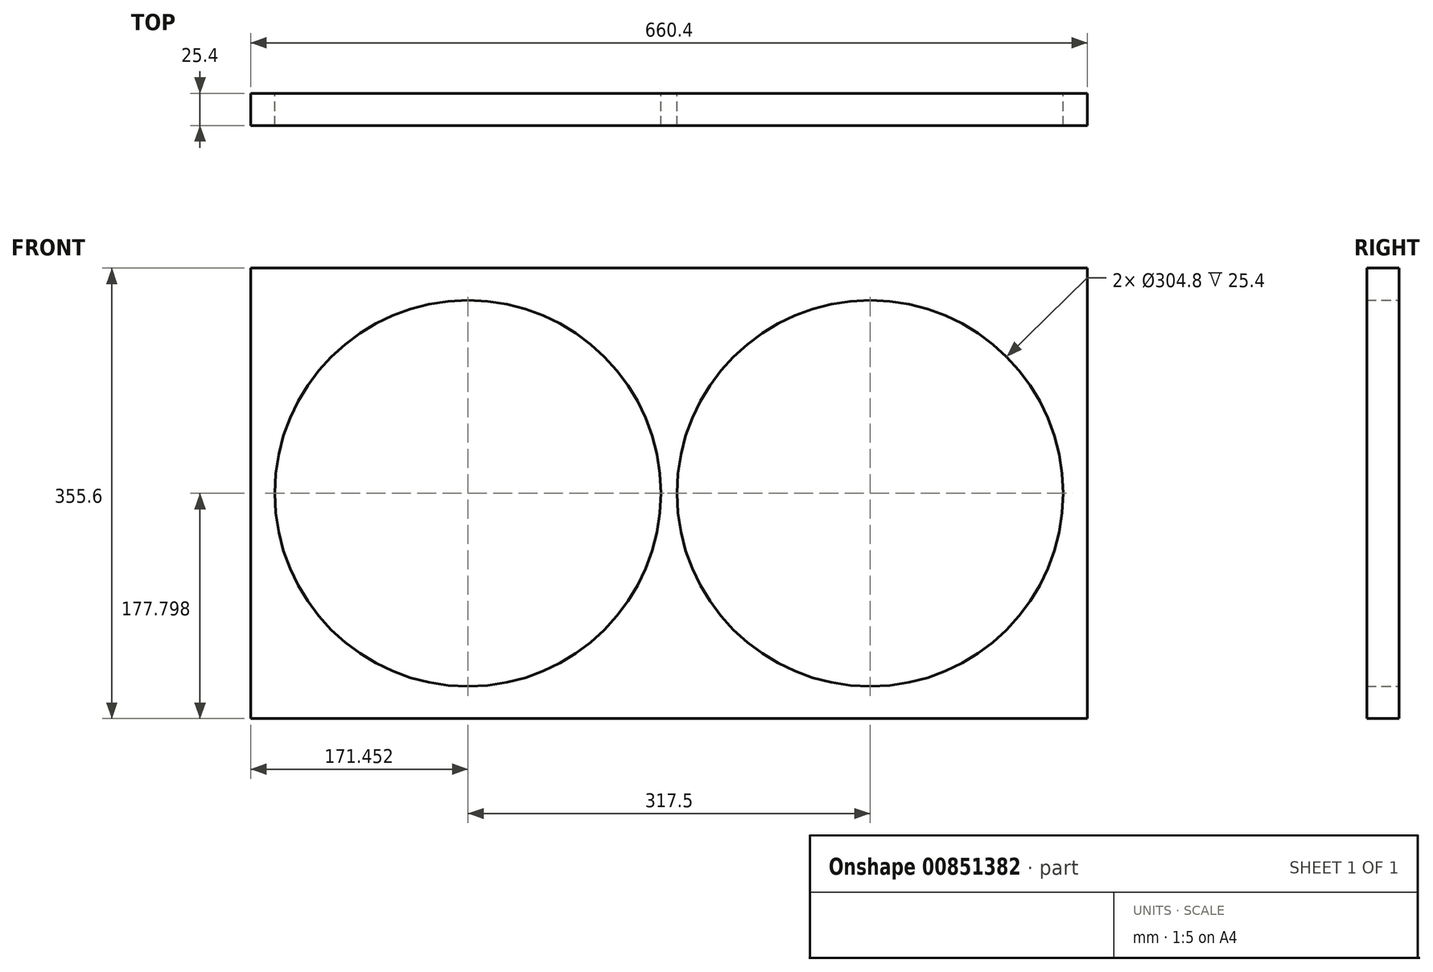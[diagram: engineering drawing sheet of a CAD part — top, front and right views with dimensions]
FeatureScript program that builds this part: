
annotation { "Feature Type Name" : "Feature", "Feature Type Description" : "" }
export const myFeature = defineFeature(function(context is Context, id is Id, definition is map)
    precondition{}
    {
        {
            var Q0;
            Q0=qCreatedBy(makeId("Front.planeOp"),FACE);
            var sketch = newSketch(context, id + "F0", { "sketchPlane" : qUnion([Q0])});
            skCircle(sketch, "E0", {"center": v(-259.39, -89.01) * mm, "radius": 152.4 * mm});
            skCircle(sketch, "E1", {"center": v(58.11, -89.01) * mm, "radius": 152.4 * mm});
            skLineSegment(sketch, "E2.bottom", {"start": v(-430.84, 88.79) * mm, "end": v(229.56, 88.79) * mm});
            skLineSegment(sketch, "E2.top", {"start": v(-430.84, -266.81) * mm, "end": v(229.56, -266.81) * mm});
            skLineSegment(sketch, "E2.left", {"start": v(-430.84, 88.79) * mm, "end": v(-430.84, -266.81) * mm});
            skLineSegment(sketch, "E2.right", {"start": v(229.56, 88.79) * mm, "end": v(229.56, -266.81) * mm});
            skPoint(sketch, "E3.firstSnap0", {"position": v(-430.84, -89.01) * mm});
            skLineSegment(sketch, "E4.left", {"start": v(-430.84, 88.79) * mm, "end": v(-430.84, -266.42) * mm});
            skSolve(sketch);
        }
        {
            var Q0;
            Q0 = qSketchRegion(id + "F0", true);
            extrude(context, id + "F1", {"entities" : qUnion([Q0]), "depth" : 25.4 * mm, "offsetDistance" : 25.4 * mm});
        }
    });
